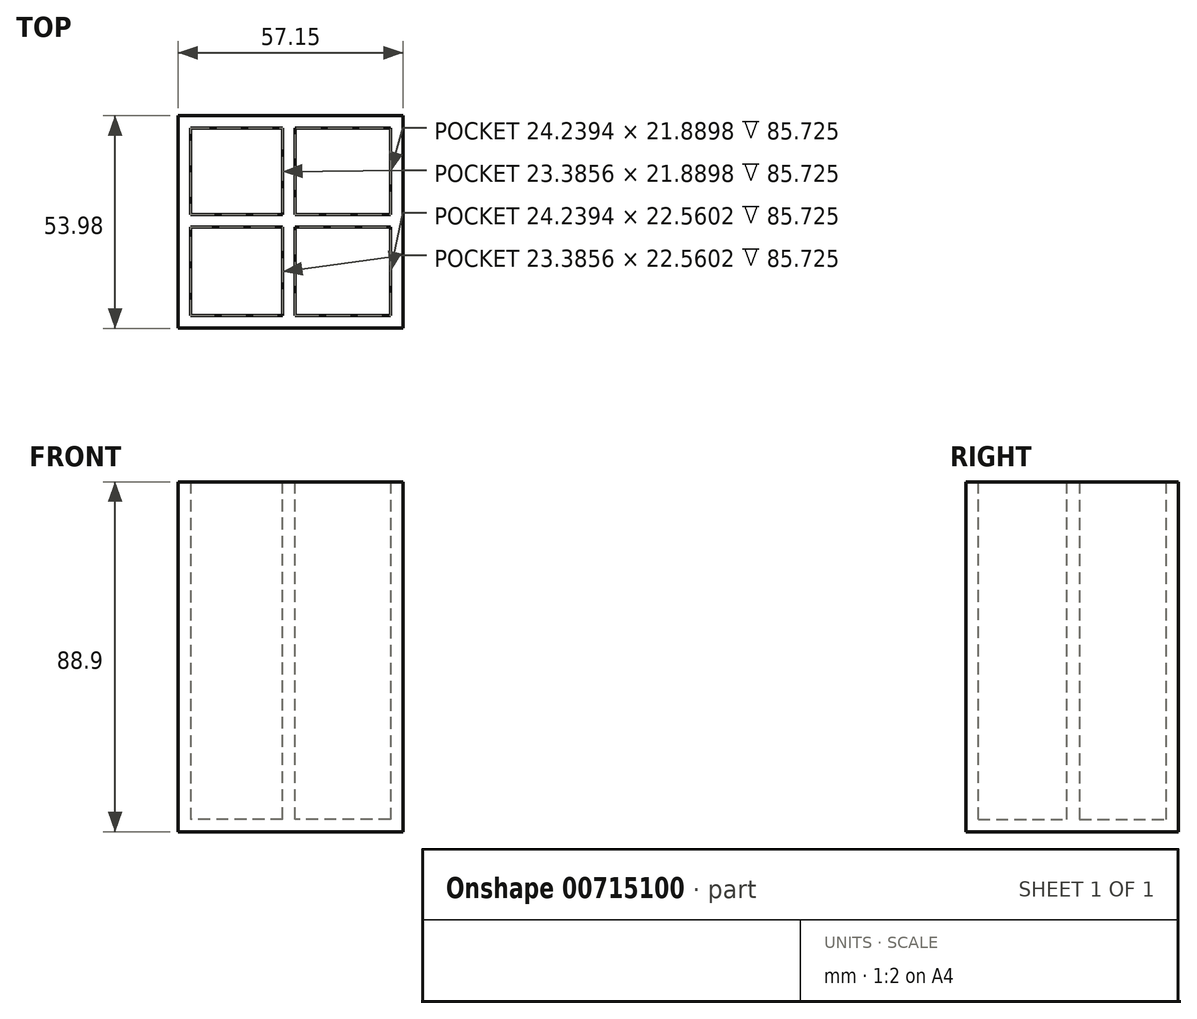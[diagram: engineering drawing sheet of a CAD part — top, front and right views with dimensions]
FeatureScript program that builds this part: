
annotation { "Feature Type Name" : "Feature", "Feature Type Description" : "" }
export const myFeature = defineFeature(function(context is Context, id is Id, definition is map)
    precondition{}
    {
        {
            var Q0;
            Q0=qCreatedBy(makeId("Front.planeOp"),FACE);
            var sketch = newSketch(context, id + "F0", { "sketchPlane" : qUnion([Q0])});
            skLineSegment(sketch, "E0.bottom", {"start": v(-21.72, 53.05) * mm, "end": v(35.43, 53.05) * mm});
            skLineSegment(sketch, "E0.top", {"start": v(-21.72, -35.85) * mm, "end": v(35.43, -35.85) * mm});
            skLineSegment(sketch, "E0.left", {"start": v(-21.72, 53.05) * mm, "end": v(-21.72, -35.85) * mm});
            skLineSegment(sketch, "E0.right", {"start": v(35.43, 53.05) * mm, "end": v(35.43, -35.85) * mm});
            skSolve(sketch);
        }
        {
            var Q0;
            Q0=makeQuery(id+"F0.imprint","IMPRINT",FACE,{"disambiguationData":[TD([[makeQuery(id+"F0.imprint","IMPRINT",EDGE,{"derivedFrom":sQuery(id+"F0.wireOp",EDGE,"E0.bottom")}),-1.0]])]});
            extrude(context, id + "F1", {"entities" : qUnion([Q0]), "depth" : 3.17 * mm, "offsetDistance" : 25.4 * mm});
        }
        {
            var Q0;
            Q0=makeQuery(id+"F1.opExtrude","CAP_FACE",FACE,{"disambiguationData":[OSD([sQuery(id+"F0.wireOp",EDGE,"E0.bottom"),sQuery(id+"F0.wireOp",EDGE,"E0.top"),sQuery(id+"F0.wireOp",EDGE,"E0.left"),sQuery(id+"F0.wireOp",EDGE,"E0.right")])],"isStart":false});
            var sketch = newSketch(context, id + "F2", { "sketchPlane" : qUnion([Q0])});
            skLineSegment(sketch, "E1.bottom", {"start": v(-21.72, 53.05) * mm, "end": v(-18.54, 53.05) * mm});
            skLineSegment(sketch, "E1.top", {"start": v(-21.72, -35.85) * mm, "end": v(-18.54, -35.85) * mm});
            skLineSegment(sketch, "E1.left", {"start": v(-21.72, 53.05) * mm, "end": v(-21.72, -35.85) * mm});
            skLineSegment(sketch, "E1.right", {"start": v(-18.54, 53.05) * mm, "end": v(-18.54, -35.85) * mm});
            skSolve(sketch);
        }
        {
            var Q0;
            Q0=makeQuery(id+"F2.imprint","IMPRINT",FACE,{"disambiguationData":[TD([[makeQuery(id+"F2.imprint","IMPRINT",EDGE,{"derivedFrom":sQuery(id+"F2.wireOp",EDGE,"E1.bottom")}),-1.0]])]});
            extrude(context, id + "F3", {"entities" : qUnion([Q0]), "operationType" : NewBodyOperationType.ADD, "depth" : 50.8 * mm, "offsetDistance" : 25.4 * mm});
        }
        {
            var Q0;
            Q0=makeQuery(id+"F1.opExtrude","CAP_FACE",FACE,{"disambiguationData":[OSD([sQuery(id+"F0.wireOp",EDGE,"E0.bottom"),sQuery(id+"F0.wireOp",EDGE,"E0.top"),sQuery(id+"F0.wireOp",EDGE,"E0.left"),sQuery(id+"F0.wireOp",EDGE,"E0.right")])],"isStart":false});
            var sketch = newSketch(context, id + "F4", { "sketchPlane" : qUnion([Q0])});
            skLineSegment(sketch, "E2.bottom", {"start": v(35.43, 53.05) * mm, "end": v(32.26, 53.05) * mm});
            skLineSegment(sketch, "E2.top", {"start": v(35.43, -35.85) * mm, "end": v(32.26, -35.85) * mm});
            skLineSegment(sketch, "E2.left", {"start": v(35.43, 53.05) * mm, "end": v(35.43, -35.85) * mm});
            skLineSegment(sketch, "E2.right", {"start": v(32.26, 53.05) * mm, "end": v(32.26, -35.85) * mm});
            skSolve(sketch);
        }
        {
            var Q0;
            Q0=makeQuery(id+"F4.imprint","IMPRINT",FACE,{"disambiguationData":[TD([[makeQuery(id+"F4.imprint","IMPRINT",EDGE,{"derivedFrom":sQuery(id+"F4.wireOp",EDGE,"E2.bottom")}),-1.0]])]});
            extrude(context, id + "F5", {"entities" : qUnion([Q0]), "operationType" : NewBodyOperationType.ADD, "depth" : 50.8 * mm, "offsetDistance" : 25.4 * mm});
        }
        {
            var Q0;
            Q0=makeQuery(id+"F5.opExtrude","CAP_FACE",FACE,{"disambiguationData":[OSD([sQuery(id+"F4.wireOp",EDGE,"E2.bottom"),sQuery(id+"F4.wireOp",EDGE,"E2.top"),sQuery(id+"F4.wireOp",EDGE,"E2.left"),sQuery(id+"F4.wireOp",EDGE,"E2.right")])],"isStart":false});
            var sketch = newSketch(context, id + "F6", { "sketchPlane" : qUnion([Q0])});
            skLineSegment(sketch, "E3.bottom", {"start": v(35.43, 53.05) * mm, "end": v(-20.8, 53.05) * mm});
            skLineSegment(sketch, "E3.top", {"start": v(35.43, -35.85) * mm, "end": v(-20.8, -35.85) * mm});
            skLineSegment(sketch, "E3.left", {"start": v(35.43, 53.05) * mm, "end": v(35.43, -35.85) * mm});
            skLineSegment(sketch, "E3.right", {"start": v(-20.8, 53.05) * mm, "end": v(-20.8, -35.85) * mm});
            skSolve(sketch);
        }
        {
            var Q0;
            {var subQ2=sQuery(id+"F6.wireOp",EDGE,"E3.right");Q0=makeQuery(id+"F6.imprint","IMPRINT",FACE,{"disambiguationData":[TD([[makeQuery(id+"F6.imprint","IMPRINT",EDGE,{"derivedFrom":subQ2}),1.0]])]});}
            extrude(context, id + "F7", {"entities" : qUnion([Q0]), "operationType" : NewBodyOperationType.ADD, "oppositeDirection" : true, "depth" : 3.17 * mm, "offsetDistance" : 25.4 * mm});
        }
        {
            var Q0;
            Q0=makeQuery(id+"F7.boolean.opBoolean","MERGE",FACE,{"derivedFrom":[makeQuery(id+"F5.boolean.opBoolean","MERGE",FACE,{"derivedFrom":[makeQuery(id+"F3.boolean.opBoolean","MERGE",FACE,{"derivedFrom":[makeQuery(id+"F1.opExtrude","SWEPT_FACE",FACE,{"disambiguationData":[OSD([sQuery(id+"F0.wireOp",EDGE,"E0.top")])]}),makeQuery(id+"F3.opExtrude","SWEPT_FACE",FACE,{"disambiguationData":[OSD([sQuery(id+"F2.wireOp",EDGE,"E1.top")])]})]}),makeQuery(id+"F5.opExtrude","SWEPT_FACE",FACE,{"disambiguationData":[OSD([sQuery(id+"F4.wireOp",EDGE,"E2.top")])]})]}),makeQuery(id+"F7.opExtrude","SWEPT_FACE",FACE,{"disambiguationData":[OSD([sQuery(id+"F6.wireOp",EDGE,"E3.top")])]})]});
            var sketch = newSketch(context, id + "F8", { "sketchPlane" : qUnion([Q0])});
            skLineSegment(sketch, "E4.bottom", {"start": v(-18.54, 3.18) * mm, "end": v(32.26, 3.18) * mm});
            skLineSegment(sketch, "E4.top", {"start": v(-18.54, 50.8) * mm, "end": v(32.26, 50.8) * mm});
            skLineSegment(sketch, "E4.left", {"start": v(-18.54, 3.18) * mm, "end": v(-18.54, 50.8) * mm});
            skLineSegment(sketch, "E4.right", {"start": v(32.26, 3.18) * mm, "end": v(32.26, 50.8) * mm});
            skSolve(sketch);
        }
        {
            var Q0;
            Q0=makeQuery(id+"F8.imprint","IMPRINT",FACE,{"disambiguationData":[TD([[makeQuery(id+"F8.imprint","IMPRINT",EDGE,{"derivedFrom":sQuery(id+"F8.wireOp",EDGE,"E4.bottom")}),1.0]])]});
            extrude(context, id + "F9", {"entities" : qUnion([Q0]), "oppositeDirection" : true, "depth" : 3.17 * mm, "offsetDistance" : 25.4 * mm});
        }
        {
            var Q0;
            Q0=makeQuery(id+"F9.opExtrude","SWEPT_BODY",BODY,{"disambiguationData":[OSD([sQuery(id+"F8.wireOp",EDGE,"E4.bottom"),sQuery(id+"F8.wireOp",EDGE,"E4.top"),sQuery(id+"F8.wireOp",EDGE,"E4.left"),sQuery(id+"F8.wireOp",EDGE,"E4.right")])]});
            deleteBodies(context, id + "F10", {"entities" : qUnion([Q0])});
        }
        {
            var Q0;
            Q0=makeQuery(id+"F7.boolean.opBoolean","MERGE",FACE,{"derivedFrom":[makeQuery(id+"F5.boolean.opBoolean","MERGE",FACE,{"derivedFrom":[makeQuery(id+"F3.boolean.opBoolean","MERGE",FACE,{"derivedFrom":[makeQuery(id+"F1.opExtrude","SWEPT_FACE",FACE,{"disambiguationData":[OSD([sQuery(id+"F0.wireOp",EDGE,"E0.top")])]}),makeQuery(id+"F3.opExtrude","SWEPT_FACE",FACE,{"disambiguationData":[OSD([sQuery(id+"F2.wireOp",EDGE,"E1.top")])]})]}),makeQuery(id+"F5.opExtrude","SWEPT_FACE",FACE,{"disambiguationData":[OSD([sQuery(id+"F4.wireOp",EDGE,"E2.top")])]})]}),makeQuery(id+"F7.opExtrude","SWEPT_FACE",FACE,{"disambiguationData":[OSD([sQuery(id+"F6.wireOp",EDGE,"E3.top")])]})]});
            var sketch = newSketch(context, id + "F11", { "sketchPlane" : qUnion([Q0])});
            skLineSegment(sketch, "E5.bottom", {"start": v(-21.72, 53.98) * mm, "end": v(35.43, 53.98) * mm});
            skLineSegment(sketch, "E5.top", {"start": v(-21.72, 0) * mm, "end": v(35.43, 0) * mm});
            skLineSegment(sketch, "E5.left", {"start": v(-21.72, 53.98) * mm, "end": v(-21.72, 0) * mm});
            skLineSegment(sketch, "E5.right", {"start": v(35.43, 53.98) * mm, "end": v(35.43, 0) * mm});
            skSolve(sketch);
        }
        {
            var Q0;
            {var subQ0=sQuery(id+"F0.wireOp",EDGE,"E0.top");Q0=makeQuery(id+"F11.imprint","IMPRINT",FACE,{"disambiguationData":[TD([[makeQuery(id+"F11.imprint","IMPRINT",EDGE,{"derivedFrom":makeQuery(id+"F1.opExtrude","CAP_EDGE",EDGE,{"disambiguationData":[OSD([subQ0])],"isStart":false})}),1.0]])]});}
            extrude(context, id + "F12", {"entities" : qUnion([Q0]), "operationType" : NewBodyOperationType.ADD, "oppositeDirection" : true, "depth" : 3.17 * mm, "offsetDistance" : 25.4 * mm});
        }
        {
            var Q0;
            Q0=makeQuery(id+"F1.opExtrude","CAP_FACE",FACE,{"disambiguationData":[OSD([sQuery(id+"F0.wireOp",EDGE,"E0.bottom"),sQuery(id+"F0.wireOp",EDGE,"E0.top"),sQuery(id+"F0.wireOp",EDGE,"E0.left"),sQuery(id+"F0.wireOp",EDGE,"E0.right")])],"isStart":false});
            var sketch = newSketch(context, id + "F13", { "sketchPlane" : qUnion([Q0])});
            skLineSegment(sketch, "E6.bottom", {"start": v(4.84, 53.05) * mm, "end": v(8.02, 53.05) * mm});
            skLineSegment(sketch, "E6.top", {"start": v(4.84, -32.68) * mm, "end": v(8.02, -32.68) * mm});
            skLineSegment(sketch, "E6.left", {"start": v(4.84, 53.05) * mm, "end": v(4.84, -32.68) * mm});
            skLineSegment(sketch, "E6.right", {"start": v(8.02, 53.05) * mm, "end": v(8.02, -32.68) * mm});
            skSolve(sketch);
        }
        {
            var Q0;
            Q0=makeQuery(id+"F13.imprint","IMPRINT",FACE,{"disambiguationData":[TD([[makeQuery(id+"F13.imprint","IMPRINT",EDGE,{"derivedFrom":sQuery(id+"F13.wireOp",EDGE,"E6.bottom")}),-1.0]])]});
            extrude(context, id + "F14", {"entities" : qUnion([Q0]), "operationType" : NewBodyOperationType.ADD, "depth" : 50.8 * mm, "offsetDistance" : 25.4 * mm});
        }
        {
            var Q0;
            Q0=makeQuery(id+"F3.opExtrude","SWEPT_FACE",FACE,{"disambiguationData":[OSD([sQuery(id+"F2.wireOp",EDGE,"E1.right")])]});
            var sketch = newSketch(context, id + "F15", { "sketchPlane" : qUnion([Q0])});
            skLineSegment(sketch, "E7.bottom", {"start": v(-28.24, 53.05) * mm, "end": v(-25.06, 53.05) * mm});
            skLineSegment(sketch, "E7.top", {"start": v(-28.24, -32.68) * mm, "end": v(-25.06, -32.68) * mm});
            skLineSegment(sketch, "E7.left", {"start": v(-28.24, 53.05) * mm, "end": v(-28.24, -32.68) * mm});
            skLineSegment(sketch, "E7.right", {"start": v(-25.06, 53.05) * mm, "end": v(-25.06, -32.68) * mm});
            skSolve(sketch);
        }
        {
            var Q0;
            Q0=makeQuery(id+"F15.imprint","IMPRINT",FACE,{"disambiguationData":[TD([[makeQuery(id+"F15.imprint","IMPRINT",EDGE,{"derivedFrom":sQuery(id+"F15.wireOp",EDGE,"E7.bottom")}),-1.0]])]});
            extrude(context, id + "F16", {"entities" : qUnion([Q0]), "operationType" : NewBodyOperationType.ADD, "depth" : 50.8 * mm, "offsetDistance" : 25.4 * mm});
        }
    });
